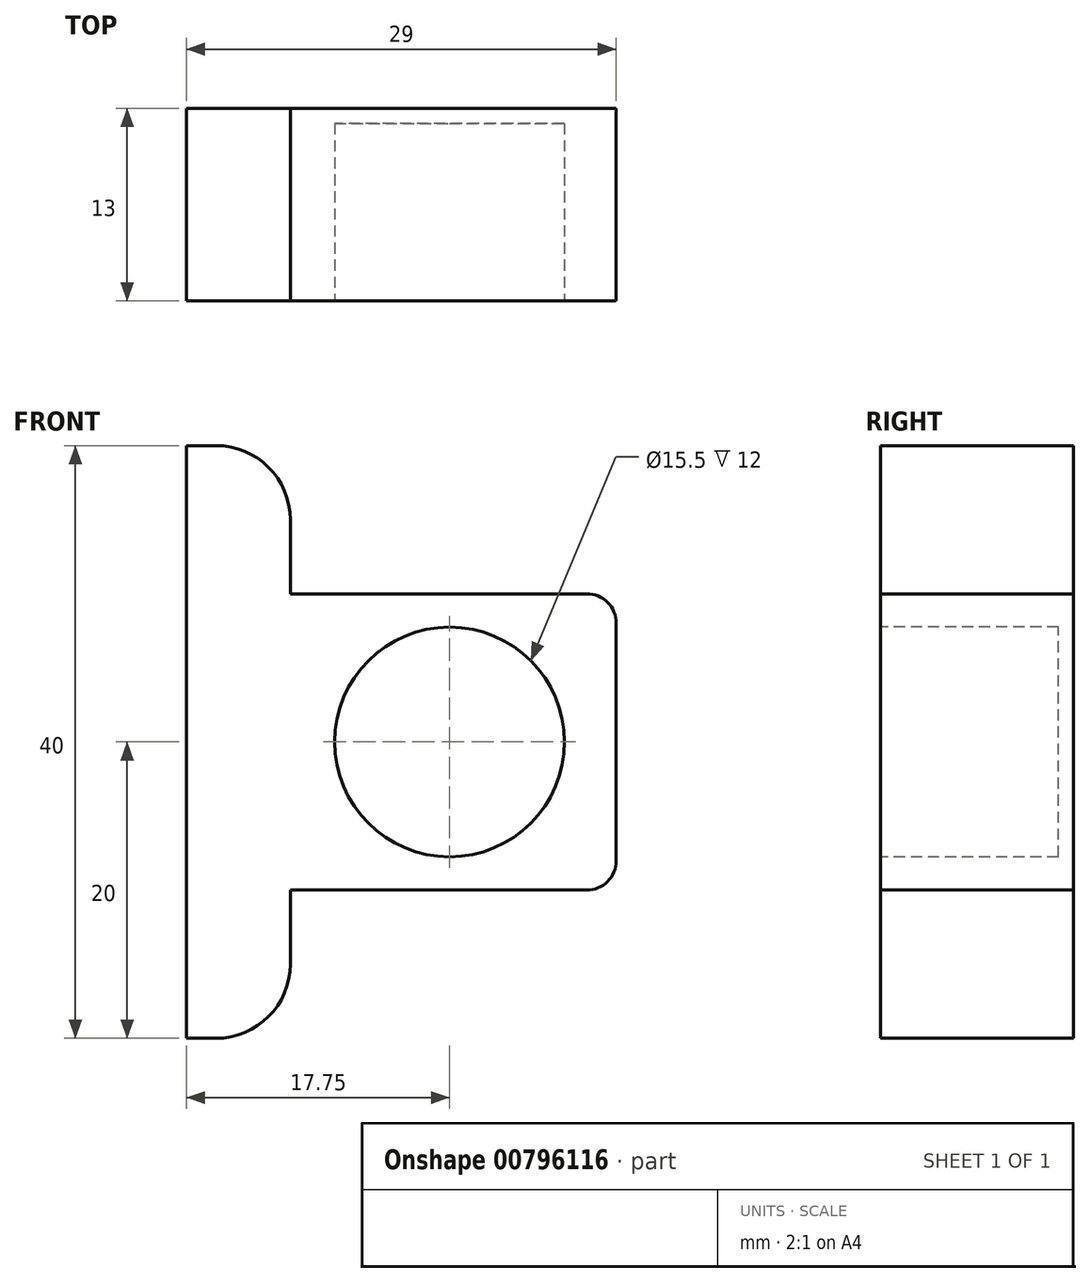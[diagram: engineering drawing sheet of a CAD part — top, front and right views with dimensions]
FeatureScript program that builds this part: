
annotation { "Feature Type Name" : "Feature", "Feature Type Description" : "" }
export const myFeature = defineFeature(function(context is Context, id is Id, definition is map)
    precondition{}
    {
        {
            var Q0;
            Q0=qCreatedBy(makeId("Top.planeOp"),FACE);
            var sketch = newSketch(context, id + "F0", { "sketchPlane" : qUnion([Q0])});
            skLineSegment(sketch, "E0", {"start": v(0, 0) * mm, "end": v(0, 13) * mm});
            skLineSegment(sketch, "E1", {"start": v(0, 13) * mm, "end": v(29, 13) * mm});
            skLineSegment(sketch, "E2", {"start": v(29, 13) * mm, "end": v(29, 0) * mm});
            skLineSegment(sketch, "E3", {"start": v(29, 0) * mm, "end": v(0, 0) * mm});
            skSolve(sketch);
        }
        {
            var Q0;
            Q0=makeQuery(id+"F0.imprint","IMPRINT",FACE,{"disambiguationData":[TD([[makeQuery(id+"F0.imprint","IMPRINT",EDGE,{"derivedFrom":sQuery(id+"F0.wireOp",EDGE,"E0")}),-1.0]])]});
            extrude(context, id + "F1", {"entities" : qUnion([Q0]), "depth" : 20 * mm, "offsetDistance" : 25 * mm});
        }
        {
            var Q0;
            Q0=makeQuery(id+"F1.opExtrude","SWEPT_FACE",FACE,{"disambiguationData":[OSD([sQuery(id+"F0.wireOp",EDGE,"E3")])]});
            var sketch = newSketch(context, id + "F2", { "sketchPlane" : qUnion([Q0])});
            skLineSegment(sketch, "E4", {"start": v(29, 20) * mm, "end": v(29, 0) * mm, "construction": true});
            skLineSegment(sketch, "E5", {"start": v(0, 20) * mm, "end": v(17.75, 10) * mm, "construction": true});
            skLineSegment(sketch, "E6", {"start": v(17.75, 10) * mm, "end": v(14.5, 20) * mm, "construction": true});
            skLineSegment(sketch, "E7", {"start": v(14.5, 0) * mm, "end": v(17.75, 10) * mm, "construction": true});
            skLineSegment(sketch, "E8", {"start": v(17.75, 10) * mm, "end": v(0, 10) * mm, "construction": true});
            skLineSegment(sketch, "E9", {"start": v(0, 10) * mm, "end": v(14.5, 20) * mm, "construction": true});
            skLineSegment(sketch, "E10", {"start": v(0, 10) * mm, "end": v(14.5, 0) * mm, "construction": true});
            skLineSegment(sketch, "E11", {"start": v(7.25, 15) * mm, "end": v(7.25, 5) * mm, "construction": true});
            skLineSegment(sketch, "E12", {"start": v(7.25, 5) * mm, "end": v(18.5, 5) * mm, "construction": true});
            skLineSegment(sketch, "E13", {"start": v(18.5, 5) * mm, "end": v(18.5, 15) * mm, "construction": true});
            skLineSegment(sketch, "E14", {"start": v(18.5, 15) * mm, "end": v(7.25, 15) * mm, "construction": true});
            skCircle(sketch, "E15", {"center": v(17.75, 10) * mm, "radius": 7.75 * mm});
            skSolve(sketch);
        }
        {
            var Q0;
            Q0=makeQuery(id+"F2.imprint","IMPRINT",FACE,{"disambiguationData":[TD([[makeQuery(id+"F2.imprint","IMPRINT",EDGE,{"derivedFrom":sQuery(id+"F2.wireOp",EDGE,"E15")}),1.0]])]});
            var Q1;
            Q1=sQuery(id+"F2.wireOp",EDGE,"E15");
            extrude(context, id + "F3", {"entities" : qUnion([Q0]), "operationType" : NewBodyOperationType.REMOVE, "surfaceOperationType" : NewSurfaceOperationType.ADD, "surfaceEntities" : qUnion([Q1]), "oppositeDirection" : true, "depth" : 12 * mm, "hasOffset" : true, "offsetDistance" : 12 * mm});
        }
        {
            var Q0;
            Q0=makeQuery(id+"F1.opExtrude","CAP_FACE",FACE,{"disambiguationData":[OSD([sQuery(id+"F0.wireOp",EDGE,"E0"),sQuery(id+"F0.wireOp",EDGE,"E1"),sQuery(id+"F0.wireOp",EDGE,"E2"),sQuery(id+"F0.wireOp",EDGE,"E3")])],"isStart":false});
            var sketch = newSketch(context, id + "F4", { "sketchPlane" : qUnion([Q0])});
            skLineSegment(sketch, "E16", {"start": v(2, 13) * mm, "end": v(2, 13) * mm});
            skLineSegment(sketch, "E17", {"start": v(7, 0) * mm, "end": v(2, 0) * mm});
            skLineSegment(sketch, "E18", {"start": v(2, 0) * mm, "end": v(2, 0) * mm});
            skLineSegment(sketch, "E19", {"start": v(7, 0) * mm, "end": v(7, 13) * mm});
            skLineSegment(sketch, "E20", {"start": v(7, 13) * mm, "end": v(0, 13) * mm});
            skLineSegment(sketch, "E21", {"start": v(0, 13) * mm, "end": v(0, 0) * mm});
            skLineSegment(sketch, "E22", {"start": v(0, 0) * mm, "end": v(7, 0) * mm});
            skSolve(sketch);
        }
        {
            var Q0;
            {var subQ3=sQuery(id+"F4.wireOp",EDGE,"E21");Q0=makeQuery(id+"F4.imprint","IMPRINT",FACE,{"disambiguationData":[TD([[makeQuery(id+"F4.imprint","IMPRINT",EDGE,{"derivedFrom":subQ3}),1.0]])]});}
            var Q1;
            {var subQ0=sQuery(id+"F4.wireOp",EDGE,"E19");Q1=makeQuery(id+"F4.imprint","IMPRINT",FACE,{"disambiguationData":[TD([[makeQuery(id+"F4.imprint","IMPRINT",EDGE,{"derivedFrom":subQ0}),1.0]])]});}
            extrude(context, id + "F5", {"entities" : qUnion([Q0, Q1]), "operationType" : NewBodyOperationType.ADD, "depth" : 10 * mm, "offsetDistance" : 25 * mm});
        }
        {
            var Q0;
            Q0=makeQuery(id+"F1.opExtrude","CAP_FACE",FACE,{"disambiguationData":[OSD([sQuery(id+"F0.wireOp",EDGE,"E0"),sQuery(id+"F0.wireOp",EDGE,"E1"),sQuery(id+"F0.wireOp",EDGE,"E2"),sQuery(id+"F0.wireOp",EDGE,"E3")])],"isStart":true});
            var sketch = newSketch(context, id + "F6", { "sketchPlane" : qUnion([Q0])});
            skLineSegment(sketch, "E23", {"start": v(0, 0) * mm, "end": v(7, 0) * mm});
            skLineSegment(sketch, "E24", {"start": v(7, 0) * mm, "end": v(7, -13) * mm});
            skLineSegment(sketch, "E25", {"start": v(7, -13) * mm, "end": v(0, -13) * mm});
            skLineSegment(sketch, "E26", {"start": v(0, -13) * mm, "end": v(0, 0) * mm});
            skSolve(sketch);
        }
        {
            var Q0;
            Q0=makeQuery(id+"F6.imprint","IMPRINT",FACE,{"disambiguationData":[TD([[makeQuery(id+"F6.imprint","IMPRINT",EDGE,{"derivedFrom":sQuery(id+"F6.wireOp",EDGE,"E23")}),1.0]])]});
            extrude(context, id + "F7", {"entities" : qUnion([Q0]), "operationType" : NewBodyOperationType.ADD, "depth" : 10 * mm, "offsetDistance" : 25 * mm});
        }
        {
            var Q0;
            Q0=makeQuery(id+"F5.opExtrude","CAP_EDGE",EDGE,{"disambiguationData":[OSD([sQuery(id+"F4.wireOp",EDGE,"E19")])],"isStart":false});
            var Q1;
            Q1=makeQuery(id+"F7.opExtrude","CAP_EDGE",EDGE,{"disambiguationData":[OSD([sQuery(id+"F6.wireOp",EDGE,"E24")])],"isStart":false});
            fillet(context, id + "F8", {"entities" : qUnion([Q0, Q1]), "radius" : 5 * mm, "tangentPropagation" : true, "allowEdgeOverflow" : false});
        }
        {
            var Q0;
            Q0=makeQuery(id+"F1.opExtrude","CAP_EDGE",EDGE,{"disambiguationData":[OSD([sQuery(id+"F0.wireOp",EDGE,"E2")])],"isStart":false});
            var Q1;
            Q1=makeQuery(id+"F1.opExtrude","CAP_EDGE",EDGE,{"disambiguationData":[OSD([sQuery(id+"F0.wireOp",EDGE,"E2")])],"isStart":true});
            fillet(context, id + "F9", {"entities" : qUnion([Q0, Q1]), "radius" : 2 * mm, "tangentPropagation" : true, "allowEdgeOverflow" : false});
        }
    });
